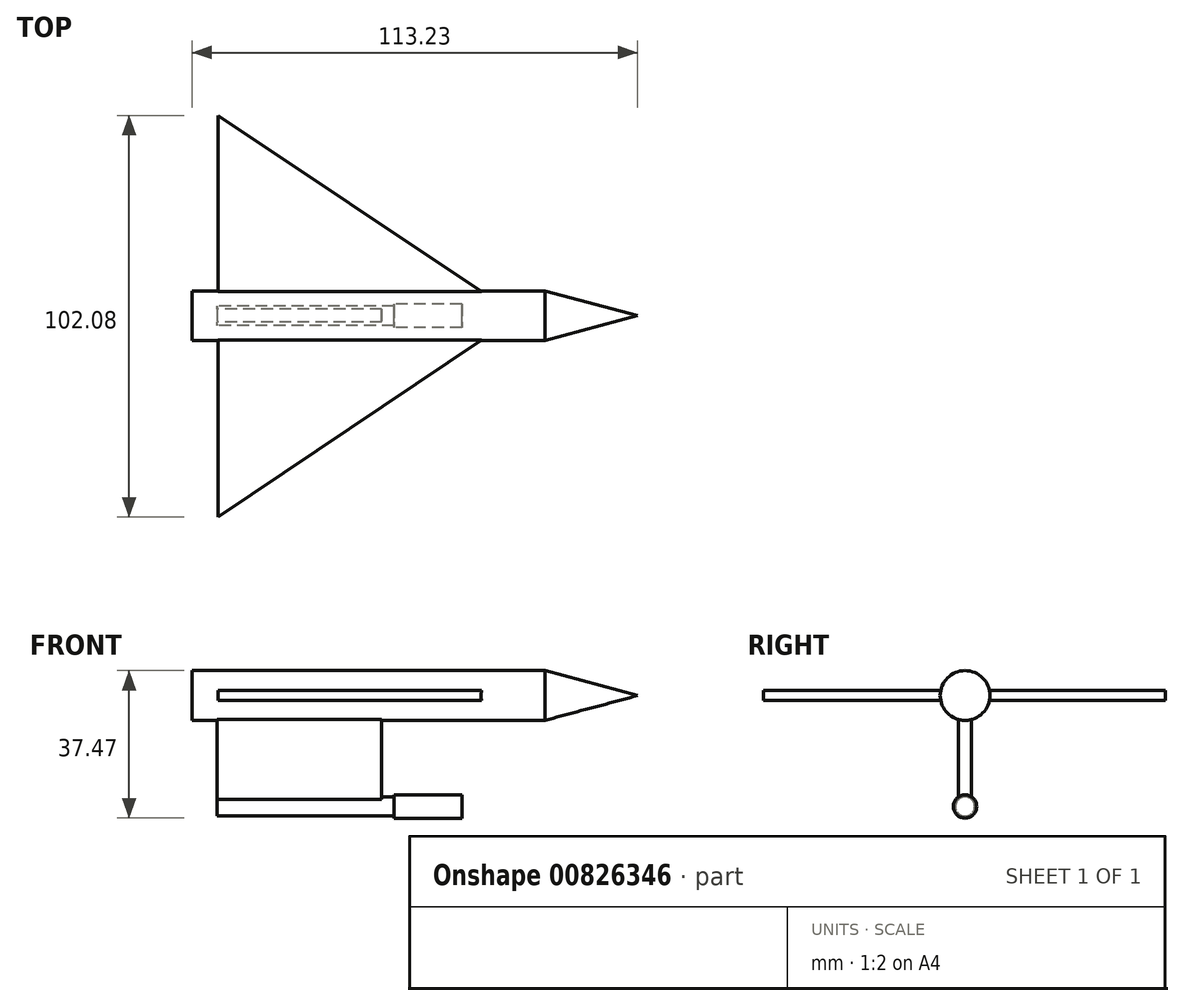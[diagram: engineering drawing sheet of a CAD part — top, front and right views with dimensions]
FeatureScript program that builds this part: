
annotation { "Feature Type Name" : "Feature", "Feature Type Description" : "" }
export const myFeature = defineFeature(function(context is Context, id is Id, definition is map)
    precondition{}
    {
        {
            var Q0;
            Q0=qCreatedBy(makeId("Top.planeOp"),FACE);
            var sketch = newSketch(context, id + "F0", { "sketchPlane" : qUnion([Q0])});
            skLineSegment(sketch, "E0", {"start": v(0, 0) * mm, "end": v(0, 50.91) * mm});
            skLineSegment(sketch, "E1", {"start": v(76.22, 0) * mm, "end": v(0, 50.91) * mm});
            skLineSegment(sketch, "E2", {"start": v(0, 0) * mm, "end": v(0, -51.17) * mm});
            skLineSegment(sketch, "E3", {"start": v(0, -51.17) * mm, "end": v(76.22, 0) * mm});
            skPoint(sketch, "E4.start.orphan", {"position": v(2.35, 0) * mm});
            skSolve(sketch);
        }
        {
            var Q0;
            Q0 = qSketchRegion(id + "F0", true);
            extrude(context, id + "F1", {"entities" : qUnion([Q0]), "depth" : 2.54 * mm, "offsetDistance" : 25.4 * mm});
        }
        {
            var Q0;
            Q0=makeQuery(id+"F1.opExtrude","SWEPT_FACE",FACE,{"disambiguationData":[OSD([sQuery(id+"F0.wireOp",EDGE,"E0"),sQuery(id+"F0.wireOp",EDGE,"E2")])]});
            var sketch = newSketch(context, id + "F2", { "sketchPlane" : qUnion([Q0])});
            skLineSegment(sketch, "E5", {"start": v(0, 0) * mm, "end": v(0, 2.54) * mm});
            skCircle(sketch, "E6", {"center": v(0, 1.27) * mm, "radius": 6.32 * mm});
            skSolve(sketch);
        }
        {
            var Q0;
            Q0 = qSketchRegion(id + "F2", true);
            extrude(context, id + "F3", {"entities" : qUnion([Q0]), "operationType" : NewBodyOperationType.ADD, "oppositeDirection" : true, "depth" : 83.06 * mm, "offsetDistance" : 25.4 * mm});
        }
        {
            var Q0;
            Q0=makeQuery(id+"F3.boolean.opBoolean","MERGE",FACE,{"derivedFrom":[makeQuery(id+"F1.opExtrude","SWEPT_FACE",FACE,{"disambiguationData":[OSD([sQuery(id+"F0.wireOp",EDGE,"E0"),sQuery(id+"F0.wireOp",EDGE,"E2")])]}),makeQuery(id+"F3.opExtrude","CAP_FACE",FACE,{"disambiguationData":[OSD([sQuery(id+"F2.wireOp",EDGE,"E6")])],"isStart":true})]});
            var sketch = newSketch(context, id + "F4", { "sketchPlane" : qUnion([Q0])});
            skLineSegment(sketch, "E7", {"start": v(0, 7.59) * mm, "end": v(0, -5.05) * mm});
            skCircle(sketch, "E8", {"center": v(0, 1.27) * mm, "radius": 6.32 * mm});
            skSolve(sketch);
        }
        {
            var Q0;
            Q0 = qSketchRegion(id + "F4", true);
            extrude(context, id + "F5", {"entities" : qUnion([Q0]), "operationType" : NewBodyOperationType.ADD, "depth" : 6.6 * mm, "offsetDistance" : 25.4 * mm});
        }
        {
            var Q0;
            Q0=makeQuery(id+"F3.opExtrude","CAP_FACE",FACE,{"disambiguationData":[OSD([sQuery(id+"F2.wireOp",EDGE,"E6")])],"isStart":false});
            extrude(context, id + "F6", {"entities" : qUnion([Q0]), "operationType" : NewBodyOperationType.ADD, "depth" : 25.4 * mm, "offsetDistance" : 25.4 * mm, "hasDraft" : true, "draftAngle" : 15 * degree, "draftPullDirection" : true});
        }
        {
            var Q0;
            {var subQ0=sQuery(id+"F0.wireOp",EDGE,"E2");var subQ1=sQuery(id+"F0.wireOp",EDGE,"E0");var subQ2=sQuery(id+"F0.wireOp",EDGE,"E3");Q0=makeQuery(id+"F3.boolean.opBoolean","SPLIT",FACE,{"disambiguationData":[TD([makeQuery(id+"F1.opExtrude","SWEPT_FACE",FACE,{"disambiguationData":[OSD([subQ2])]})])],"derivedFrom":makeQuery(id+"F1.opExtrude","CAP_FACE",FACE,{"disambiguationData":[OSD([subQ1,sQuery(id+"F0.wireOp",EDGE,"E1"),subQ0,subQ2])],"isStart":true})});}
            var sketch = newSketch(context, id + "F7", { "sketchPlane" : qUnion([Q0])});
            skLineSegment(sketch, "E9", {"start": v(41.35, 0) * mm, "end": v(0, 0) * mm});
            skPoint(sketch, "E10.middle", {"position": v(20.67, 0) * mm});
            skPoint(sketch, "E10.left.start.orphan", {"position": v(41.4, 3.65) * mm});
            skPoint(sketch, "E10.top.start.orphan", {"position": v(41.4, -3.65) * mm});
            skPoint(sketch, "E10.right.end.orphan", {"position": v(-0.06, -3.65) * mm});
            skPoint(sketch, "E10.right.start.orphan", {"position": v(-0.06, 3.65) * mm});
            skLineSegment(sketch, "E11.bottom", {"start": v(41.6, -1.64) * mm, "end": v(-0.25, -1.64) * mm});
            skLineSegment(sketch, "E11.top", {"start": v(41.6, 1.64) * mm, "end": v(-0.25, 1.64) * mm});
            skLineSegment(sketch, "E11.left", {"start": v(41.6, -1.64) * mm, "end": v(41.6, 1.64) * mm});
            skLineSegment(sketch, "E11.right", {"start": v(-0.25, -1.64) * mm, "end": v(-0.25, 1.64) * mm});
            skSolve(sketch);
        }
        {
            var Q0;
            Q0 = qSketchRegion(id + "F7", true);
            extrude(context, id + "F8", {"entities" : qUnion([Q0]), "operationType" : NewBodyOperationType.ADD, "depth" : 26.92 * mm, "offsetDistance" : 25.4 * mm});
        }
        {
            var Q0;
            Q0=makeQuery(id+"F8.opExtrude","SWEPT_FACE",FACE,{"disambiguationData":[OSD([sQuery(id+"F7.wireOp",EDGE,"E11.right")])]});
            var sketch = newSketch(context, id + "F9", { "sketchPlane" : qUnion([Q0])});
            skCircle(sketch, "E12", {"center": v(0, -26.92) * mm, "radius": 2.45 * mm});
            skSolve(sketch);
        }
        {
            var Q0;
            Q0 = qSketchRegion(id + "F9", true);
            extrude(context, id + "F10", {"entities" : qUnion([Q0]), "operationType" : NewBodyOperationType.ADD, "oppositeDirection" : true, "depth" : 44.96 * mm, "offsetDistance" : 25.4 * mm});
        }
        {
            var Q0;
            Q0=makeQuery(id+"F10.opExtrude","CAP_FACE",FACE,{"disambiguationData":[OSD([sQuery(id+"F9.wireOp",EDGE,"E12")])],"isStart":false});
            var sketch = newSketch(context, id + "F11", { "sketchPlane" : qUnion([Q0])});
            skCircle(sketch, "E13", {"center": v(0, -26.92) * mm, "radius": 2.96 * mm});
            skSolve(sketch);
        }
        {
            var Q0;
            Q0 = qSketchRegion(id + "F11", true);
            extrude(context, id + "F12", {"entities" : qUnion([Q0]), "operationType" : NewBodyOperationType.ADD, "depth" : 17.27 * mm, "offsetDistance" : 25.4 * mm});
        }
    });
